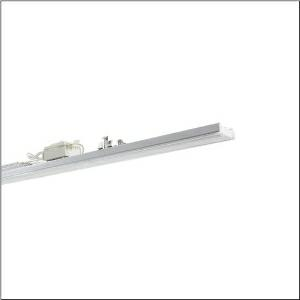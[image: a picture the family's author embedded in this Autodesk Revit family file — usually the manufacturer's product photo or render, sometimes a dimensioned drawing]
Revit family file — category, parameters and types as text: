
# Revit family: licross_r__11_recessed_ho_51tl18mn4d5m_72a7
name_source: partatom
category: Lighting Fixtures
units: mm (PartAtom-declared; Revit-internal decimal feet)

## family parameters
Cut with Voids When Loaded = No
Host = Face
Light Source = No
Part Type = Normal
Room Calculation Point = No
Round Connector Dimension = Use Diameter
Shared = No

## types (1)
- --- (1 x LED, 13950 lm, 74.5 W, 4000K)
    Apparent Load = 75 VA
    CIE Flux Codes = 78 94 99 100 100
    Color Rendering = 80
    Color Temperature = 4000K
    Default Elevation = 1800 mm
    Description = Licross® 11 Recessed HO, luminaire insert, of sheet steel, coil coated, white, length: 1.500mm, width: 66mm, height: 67mm, LED rated luminous flux: 13.950lm, light colour: 840, control gear: ON/OFF Multilumen, with plug, 3-pole, with phase selection, mains connection: 220..240V, AC, 50/60Hz, rated input power: 75W, internal wiring halogen-free, primary light control with lens, of plastic, primary optical cover: cover, of PMMA, light emission: direct distribution, primary light characteristic: symmetric, protection rating (complete): IP40, insulation class (complete): insulation class I (protective earthing), certification: CE, ENEC, VDE, UKCA, protection symbol: D if used in an environment without relevant dust loads with corresponding accessories, impact resistance: IK06, permissible ambient temperature for indoor applications: -35..+35°C, corresponds to IFS (International Featured Standards) requirements for safety and quality in the food industry, reducing of maximum allowable ambient temperature of 5°C with ceiling mounting, packaging unit: 1 piece
    Height = 58 mm
    Lamp = 1 x LED
    Lamp Light Flux = 13950 lm
    Lamp Power = 74.5 W
    Lamp count = 1
    Length = 1500 mm
    Luminous efficacy = 187 lm/W
    Manufacturer = Siteco
    ModVariant = No
    Model = 51TL18MN4D5M
    Mounting Place = Ceiling
    Mounting Type = Pendant
    Number of Poles = 1
    OnlyDefault = Yes
    Power Factor = 1
    Product Name = Licross® 11 Recessed HO
    Product group = luminaire insert | ceiling pendant
    ProductGroupID = 902
    Protection Class = Protection class I
    Protection Degree = IP 40
    RLX_Detail_Level = 1
    RLX_Emergency_Light_Flux = 0 lm
    RLX_Emergency_Type = 0
    RLX_Emergency_Type_DB = No
    RlxData = <blob elided: 22217 chars, md5=55fae663>
    Socket = socket
    Standby Power = 0 W
    System Light Flux = 13950 lm
    System Power = 75 W
    Type Comments = factory setting: luminous flux: 100 % | (A | C | E) | 174 mA
    Type Image = l_1296930.jpg
    URL = http://relux.com
    VarID = @adj_106247
    Voltage = 0 V
    Weight = 0.00 kg
    Width = 66 mm

## geometry (parser evidence)
native form markers: Blend x4, Sweep x10
no freeform markers — native parametric forms only
